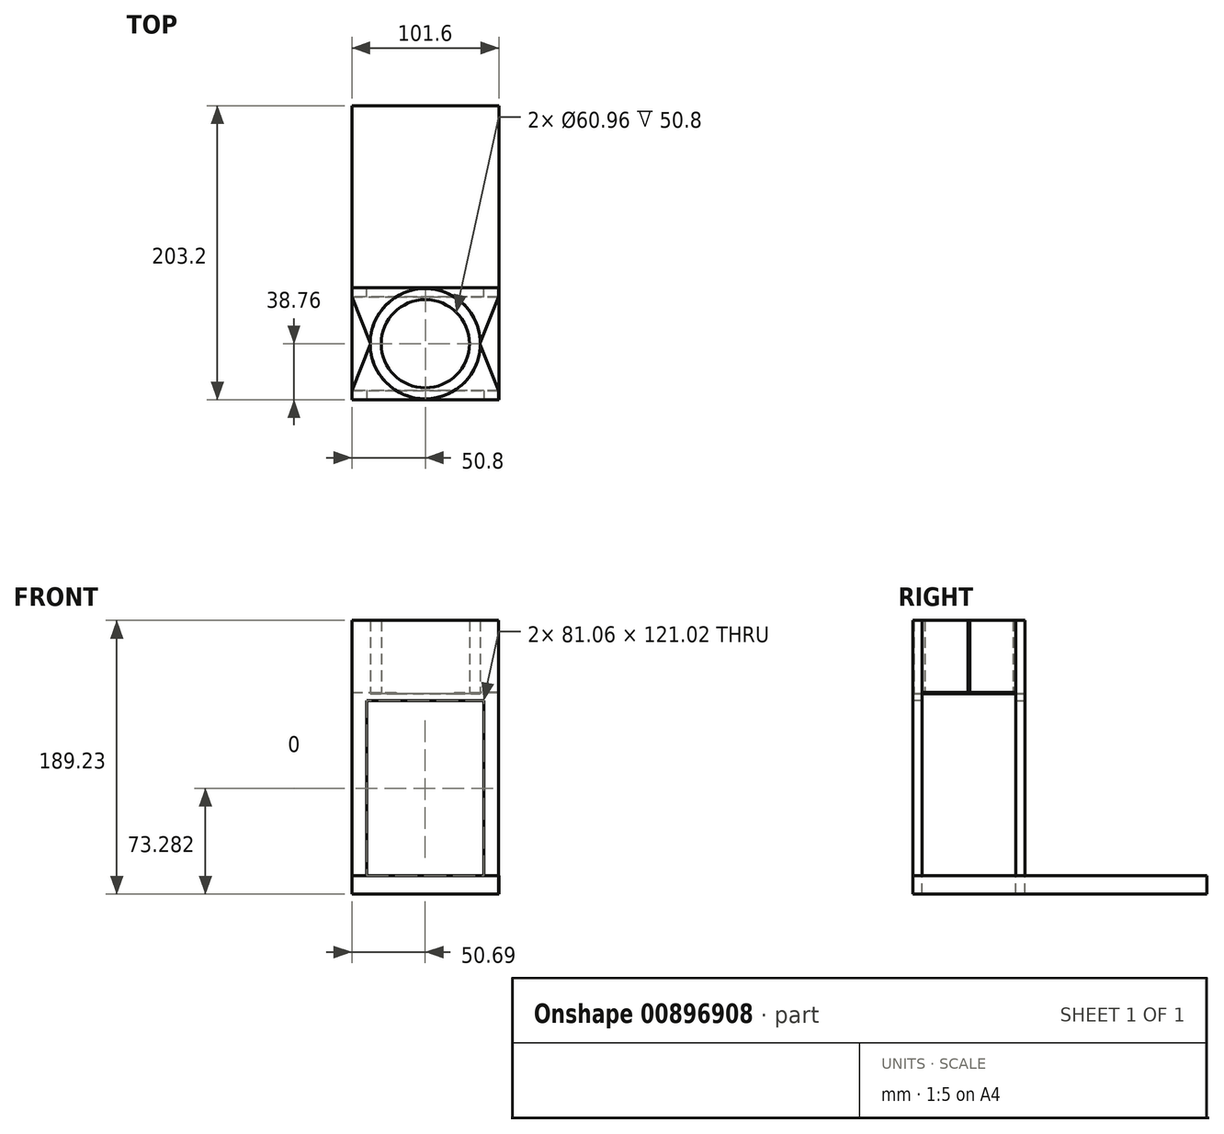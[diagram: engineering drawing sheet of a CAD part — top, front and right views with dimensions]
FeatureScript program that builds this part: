
annotation { "Feature Type Name" : "Feature", "Feature Type Description" : "" }
export const myFeature = defineFeature(function(context is Context, id is Id, definition is map)
    precondition{}
    {
        {
            var Q0;
            Q0=qCreatedBy(makeId("Top.planeOp"),FACE);
            var sketch = newSketch(context, id + "F0", { "sketchPlane" : qUnion([Q0])});
            skCircle(sketch, "E0", {"center": v(0, 0) * mm, "radius": 30.48 * mm});
            skCircle(sketch, "E1", {"center": v(0, 0) * mm, "radius": 38.1 * mm});
            skSolve(sketch);
        }
        {
            var Q0;
            Q0=makeQuery(id+"F0.imprint","IMPRINT",FACE,{"disambiguationData":[TD([[makeQuery(id+"F0.imprint","IMPRINT",EDGE,{"derivedFrom":sQuery(id+"F0.wireOp",EDGE,"E0")}),-1.0]])]});
            extrude(context, id + "F1", {"entities" : qUnion([Q0]), "depth" : 50.8 * mm, "offsetDistance" : 25.4 * mm});
        }
        {
            var Q0;
            Q0=qCreatedBy(makeId("Top.planeOp"),FACE);
            cPlane(context, id + "F2", {"entities" : qUnion([Q0]), "cplaneType" : CPlaneType.OFFSET, "offset" : 138.43 * mm, "oppositeDirection" : true, "width" : 152.4 * mm, "height" : 152.4 * mm});
        }
        {
            var Q0;
            Q0=qCreatedBy(id+"F2.planeOp",FACE);
            var sketch = newSketch(context, id + "F3", { "sketchPlane" : qUnion([Q0])});
            skLineSegment(sketch, "E2.bottom", {"start": v(50.8, 164.44) * mm, "end": v(-50.8, 164.44) * mm});
            skLineSegment(sketch, "E2.top", {"start": v(50.8, -38.76) * mm, "end": v(-50.8, -38.76) * mm});
            skLineSegment(sketch, "E2.left", {"start": v(50.8, 164.44) * mm, "end": v(50.8, -38.76) * mm});
            skLineSegment(sketch, "E2.right", {"start": v(-50.8, 164.44) * mm, "end": v(-50.8, -38.76) * mm});
            skPoint(sketch, "E2.middle", {"position": v(0, 62.84) * mm});
            skSolve(sketch);
        }
        {
            var Q0;
            Q0 = qSketchRegion(id + "F3", true);
            extrude(context, id + "F4", {"entities" : qUnion([Q0]), "depth" : 12.7 * mm, "offsetDistance" : 25.4 * mm});
        }
        {
            var Q0;
            Q0=makeQuery(id+"F4.opExtrude","SWEPT_FACE",FACE,{"disambiguationData":[OSD([sQuery(id+"F3.wireOp",EDGE,"E2.top")])]});
            var sketch = newSketch(context, id + "F5", { "sketchPlane" : qUnion([Q0])});
            skLineSegment(sketch, "E3.bottom", {"start": v(-50.8, -138.43) * mm, "end": v(50.58, -138.43) * mm});
            skLineSegment(sketch, "E3.top", {"start": v(-50.8, 50.78) * mm, "end": v(50.58, 50.78) * mm});
            skLineSegment(sketch, "E3.left", {"start": v(-50.8, -138.43) * mm, "end": v(-50.8, 50.78) * mm});
            skLineSegment(sketch, "E3.right", {"start": v(50.58, -138.43) * mm, "end": v(50.58, 50.78) * mm});
            skSolve(sketch);
        }
        {
            var Q0;
            Q0 = qSketchRegion(id + "F5", true);
            extrude(context, id + "F6", {"entities" : qUnion([Q0]), "oppositeDirection" : true, "depth" : 6.35 * mm, "offsetDistance" : 25.4 * mm});
        }
        {
            var Q0;
            Q0=makeQuery(id+"F6.opExtrude","SWEPT_FACE",FACE,{"disambiguationData":[OSD([sQuery(id+"F5.wireOp",EDGE,"E3.top")])]});
            var sketch = newSketch(context, id + "F7", { "sketchPlane" : qUnion([Q0])});
            skLineSegment(sketch, "E4", {"start": v(-50.8, -32.41) * mm, "end": v(-37.95, 0) * mm});
            skLineSegment(sketch, "E5", {"start": v(50.58, -32.41) * mm, "end": v(37.81, 0) * mm});
            skArc(sketch, "E6", {"start": v(-37.95, 0) * mm, "mid": v(-33.08, -18.6) * mm, "end": v(-19.73, -32.41) * mm});
            skLineSegment(sketch, "E7", {"start": v(-50.8, -32.41) * mm, "end": v(-19.73, -32.41) * mm});
            skLineSegment(sketch, "E8.trimOffspring", {"start": v(19.73, -32.41) * mm, "end": v(50.58, -32.41) * mm});
            skArc(sketch, "E9.trimOffspring", {"start": v(19.73, -32.41) * mm, "mid": v(33, -18.74) * mm, "end": v(37.95, -0.34) * mm});
            skSolve(sketch);
        }
        {
            var Q0;
            Q0 = qSketchRegion(id + "F7", true);
            extrude(context, id + "F8", {"entities" : qUnion([Q0]), "operationType" : NewBodyOperationType.ADD, "oppositeDirection" : true, "depth" : 49.78 * mm, "offsetDistance" : 25.4 * mm});
        }
        {
            var Q0;
            Q0=makeQuery(id+"F6.boolean.opBoolean","MERGE",FACE,{"derivedFrom":[makeQuery(id+"F4.opExtrude","SWEPT_FACE",FACE,{"disambiguationData":[OSD([sQuery(id+"F3.wireOp",EDGE,"E2.top")])]}),makeQuery(id+"F6.opExtrude","CAP_FACE",FACE,{"disambiguationData":[OSD([sQuery(id+"F5.wireOp",EDGE,"E3.bottom"),sQuery(id+"F5.wireOp",EDGE,"E3.top"),sQuery(id+"F5.wireOp",EDGE,"E3.left"),sQuery(id+"F5.wireOp",EDGE,"E3.right")])],"isStart":true})]});
            var sketch = newSketch(context, id + "F9", { "sketchPlane" : qUnion([Q0])});
            skLineSegment(sketch, "E10.bottom", {"start": v(40.42, -125.66) * mm, "end": v(-40.64, -125.66) * mm});
            skLineSegment(sketch, "E10.top", {"start": v(40.42, -4.64) * mm, "end": v(-40.64, -4.64) * mm});
            skLineSegment(sketch, "E10.left", {"start": v(40.42, -125.66) * mm, "end": v(40.42, -4.64) * mm});
            skLineSegment(sketch, "E10.right", {"start": v(-40.64, -125.66) * mm, "end": v(-40.64, -4.64) * mm});
            skSolve(sketch);
        }
        {
            var Q0;
            Q0=makeQuery(id+"F9.imprint","IMPRINT",FACE,{"disambiguationData":[TD([[makeQuery(id+"F9.imprint","IMPRINT",EDGE,{"derivedFrom":sQuery(id+"F9.wireOp",EDGE,"E10.bottom")}),-1.0]])]});
            extrude(context, id + "F10", {"entities" : qUnion([Q0]), "operationType" : NewBodyOperationType.REMOVE, "oppositeDirection" : true, "depth" : 25.4 * mm, "offsetDistance" : 25.4 * mm});
        }
        {
            var Q0;
            Q0=makeQuery(id+"F1.opExtrude","SWEPT_BODY",BODY,{"disambiguationData":[OSD([sQuery(id+"F0.wireOp",EDGE,"E0"),sQuery(id+"F0.wireOp",EDGE,"E1")])]});
            var Q1;
            Q1=qCreatedBy(makeId("Front.planeOp"),FACE);
            mirror(context, id + "F11", {"entities" : qUnion([Q0]), "mirrorPlane" : qUnion([Q1])});
        }
    });
